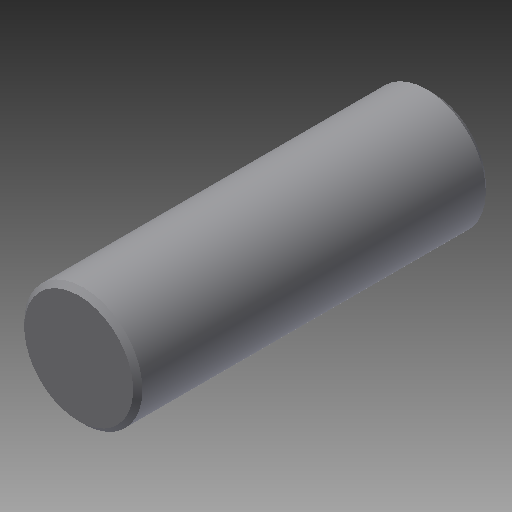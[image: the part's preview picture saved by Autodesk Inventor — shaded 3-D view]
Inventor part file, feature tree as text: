
AUTODESK INVENTOR PART (.ipt)
format: ipt  version: 2019.4 (Build 234330000, 330)  size: 119,296 bytes
history: native  units: in
note: dims shown in document units (in); Inventor stores cm internally (conversion verified against a paired STEP export)
features: other x35, revolve x1, sketch x1
ambient origin geometry x8: Origin, YZ Plane, XZ Plane, XY Plane, X Axis, Y Axis, Z Axis, Center Point
bodies: Solid1 (feature_tree)
feature tree (37):
  revolve  "Revolution1"  [1 undecoded]
  other  "dia1_XY"
  other  "dia1_YZ"
  other  "dia1_ZX"
  other  "dia1_X"
  other  "dia1_Y"
  other  "dia1_Z"
  other  "dia1_Center"
  other  "dia2_XY"
  other  "dia2_YZ"
  other  "dia2_ZX"
  other  "dia2_X"
  other  "dia2_Y"
  other  "dia2_Z"
  other  "dia2_Center"
  other  "pin_XY"
  other  "pin_YZ"
  other  "pin_ZX"
  other  "pin_X"
  other  "pin_Y"
  other  "pin_Z"
  other  "pin_Center"
  other  "pin1_XY"
  other  "pin1_YZ"
  other  "pin1_ZX"
  other  "pin1_X"
  other  "pin1_Y"
  other  "pin1_Z"
  other  "pin1_Center"
  other  "pin2_XY"
  other  "pin2_YZ"
  other  "pin2_ZX"
  other  "pin2_X"
  other  "pin2_Y"
  other  "pin2_Z"
  other  "pin2_Center"
  sketch  "Sketch_1"  dims[d0=360.0deg]
note: 1 required parameter value undecoded (feature->parameter linkage not recoverable at this tier; creation-order binding heuristic only, values carry confidence <= 0.55)
